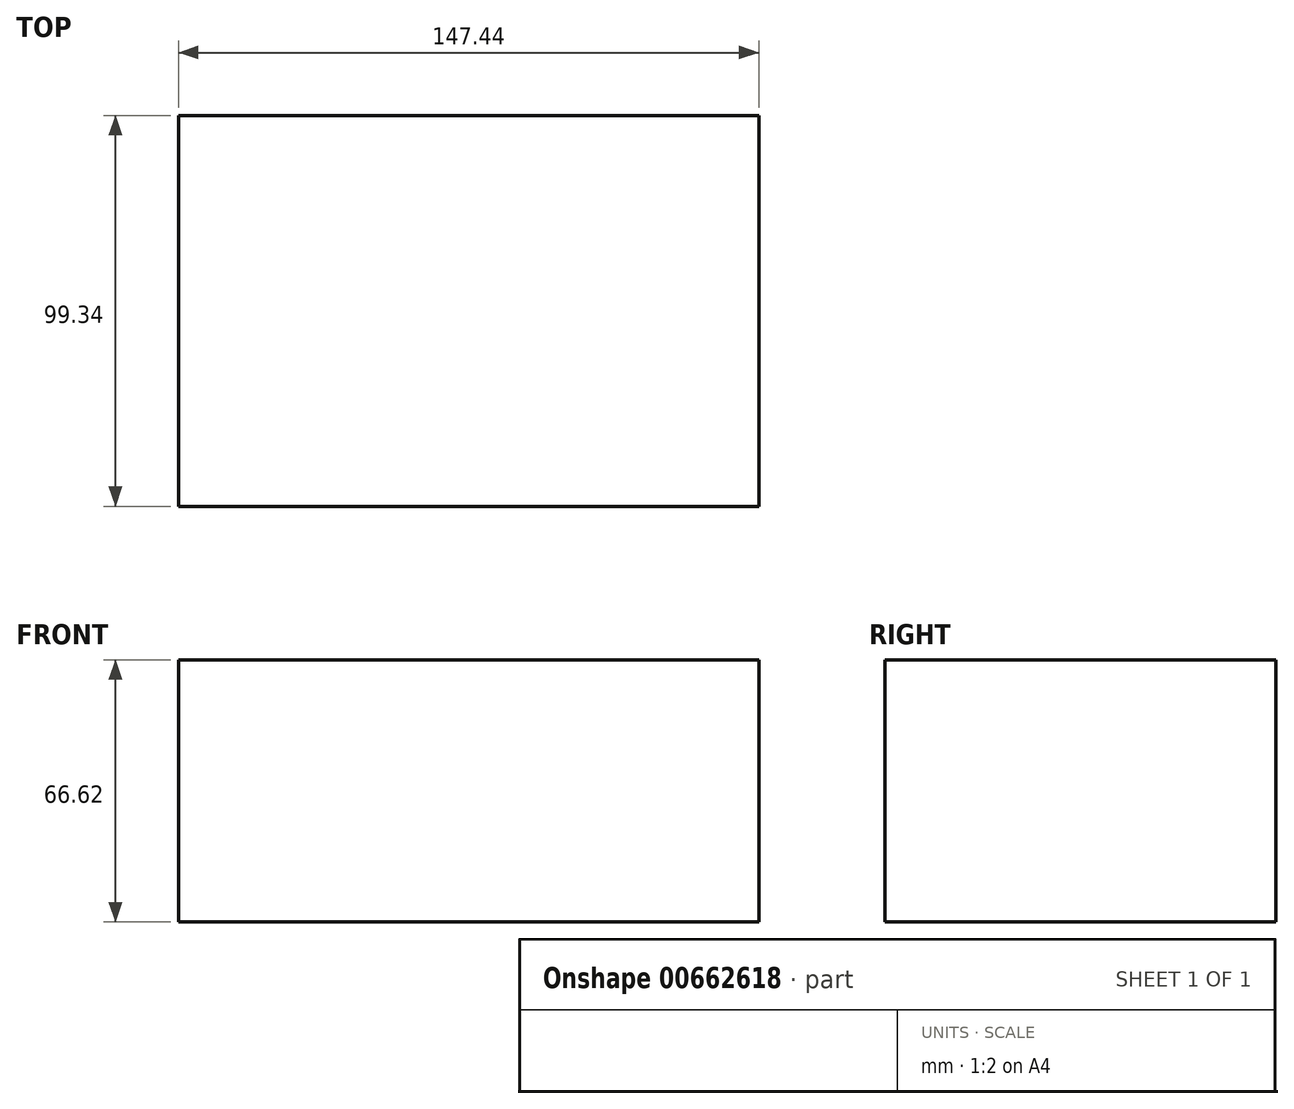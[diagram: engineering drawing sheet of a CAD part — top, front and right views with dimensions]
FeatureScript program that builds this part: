
annotation { "Feature Type Name" : "Feature", "Feature Type Description" : "" }
export const myFeature = defineFeature(function(context is Context, id is Id, definition is map)
    precondition{}
    {
        {
            var Q0;
            Q0=qCreatedBy(makeId("Top.planeOp"),FACE);
            var sketch = newSketch(context, id + "F0", { "sketchPlane" : qUnion([Q0])});
            skLineSegment(sketch, "E0.bottom", {"start": v(73.72, -49.67) * mm, "end": v(-73.72, -49.67) * mm});
            skLineSegment(sketch, "E0.top", {"start": v(73.72, 49.67) * mm, "end": v(-73.72, 49.67) * mm});
            skLineSegment(sketch, "E0.left", {"start": v(73.72, -49.67) * mm, "end": v(73.72, 49.67) * mm});
            skLineSegment(sketch, "E0.right", {"start": v(-73.72, -49.67) * mm, "end": v(-73.72, 49.67) * mm});
            skPoint(sketch, "E0.middle", {"position": v(0, 0) * mm});
            skSolve(sketch);
        }
        {
            var Q0;
            Q0=makeQuery(id+"F0.imprint","IMPRINT",FACE,{"disambiguationData":[TD([[makeQuery(id+"F0.imprint","IMPRINT",EDGE,{"derivedFrom":sQuery(id+"F0.wireOp",EDGE,"E0.bottom")}),-1.0]])]});
            extrude(context, id + "F1", {"entities" : qUnion([Q0]), "depth" : 66.62 * mm, "offsetDistance" : 25.4 * mm});
        }
    });
